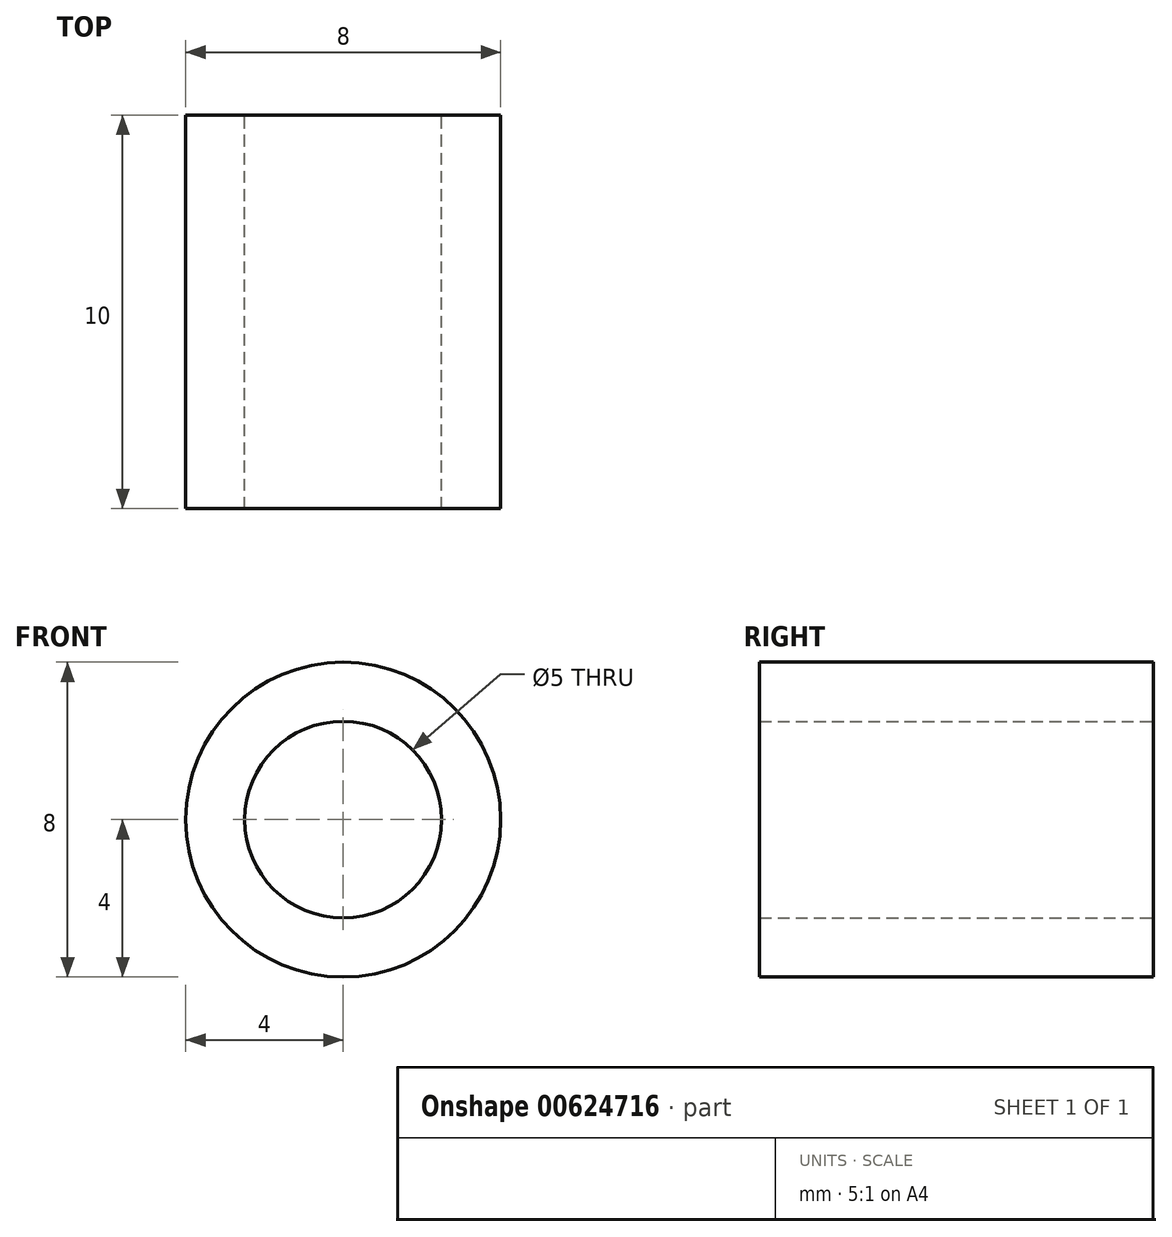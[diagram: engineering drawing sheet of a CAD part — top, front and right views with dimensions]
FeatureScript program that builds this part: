
annotation { "Feature Type Name" : "Feature", "Feature Type Description" : "" }
export const myFeature = defineFeature(function(context is Context, id is Id, definition is map)
    precondition{}
    {
        {
            var Q0;
            Q0=qCreatedBy(makeId("Front.planeOp"),FACE);
            var sketch = newSketch(context, id + "F0", { "sketchPlane" : qUnion([Q0])});
            skCircle(sketch, "E0", {"center": v(0, 0) * mm, "radius": 2.5 * mm});
            skCircle(sketch, "E1", {"center": v(0, 0) * mm, "radius": 4 * mm});
            skSolve(sketch);
        }
        {
            var Q0;
            Q0=makeQuery(id+"F0.imprint","IMPRINT",FACE,{"disambiguationData":[TD([[makeQuery(id+"F0.imprint","IMPRINT",EDGE,{"derivedFrom":sQuery(id+"F0.wireOp",EDGE,"E0")}),-1.0]])]});
            extrude(context, id + "F1", {"entities" : qUnion([Q0]), "depth" : 10 * mm, "offsetDistance" : 25 * mm});
        }
    });
